# Revit family: Hager-Volta-IP30-Surface_mounted-syst-NoHosted-DE-de
name_source: partatom
category: Electrical Equipment
units: mm (PartAtom-declared; Revit-internal decimal feet)

## family parameters
Always vertical = Yes
Cut with Voids When Loaded = No
Panel Configuration = Two Columns, Circuits Across
Part Type = Panelboard
Room Calculation Point = No
Round Connector Dimension = Use Diameter
Shared = No
Work Plane-Based = Yes

## types (6) — shared parameters
Default Elevation = 1219 mm
EF000003 - Montageart = EV000384 - Aufputz
EF000007 - Farbe = EV000202 - weiß
EF000008 - Breite = 305 mm  [stored 1.00066 ft]
EF000049 - Tiefe = 96 mm  [stored 0.314961 ft]
EF000116 - RAL-Nummer = 9010
EF001062 - EMV-Ausführung = No
EF001088 - Anbaumöglichkeit = Yes
EF001131 - Innentiefe = 92 mm
EF001134 - DIN-Schiene = Yes
EF002950 - Breite in Teilungseinheiten = 12
EF005474 - Schutzart (IP) = EV006410 - IP30
EF006244 - Transparenter Deckel/Tür = No
EF006306 - Mit Schloss = No
EF009212 - Ausführung Deckel = EV009916 - mit Ausschnitt
EF015776 - Erdungsklemmenblock = No
EF015777 - Neutralleiterklemmenblock = No
EF015941 - Signaldurchlassende Tür = No
HG000001 - Anzahl der Spalten = 1
HG000003 - Bereich = Volta
HG000005 - Dicke = 3 mm  [stored 0.00984252 ft]
HG000006 - Unterputz = No
HG000009 - Doppelflügeligen Tür = No
HG000010 - Asymmetrische Türen = No
HG000011 - Leere Reihen von unten = No
HG000017 - Distanz zwischen den Polen = 18 mm  [stored 0.0590551 ft]
Manufacturer = Hager
Type Comments = Volta
zero-valued in all types: EF000218 - Einbautiefe, EF000332 - Einbauhöhe, EF000846 - Einbaubreite, HG000007 - Anzahl der leeren Spalten, HG000008 - Anzahl der leeren Reihen

## per-type parameters (varying)
| type | EF000040 - Höhe | EF000118 - Mit Montageplatte | EF000266 - Anzahl der Reihen | EF000339 - Art der Abdeckung | EF001596 - Werkstoff des Gehäuses | EF004462 - Art der Schließung | HG000002 - Mit tür | HG000004 - Herstellerreferenz | Model |
| Aufputz IP30 B305 H245 T96.5 12 Teilungseinheiten - VA12CN | 245 mm | No | 1 | EV000494 - ohne | EV000139 - Kunststoff |  | No | VA12CN | VA12CN |
| Aufputz IP30 B305 H370 T96.5 12 Teilungseinheiten - VA24CN | 370 mm | No | 2 | EV000494 - ohne | EV000139 - Kunststoff |  | No | VA24CN | VA24CN |
| Aufputz IP30 B305 H515 T96.5 12 Teilungseinheiten - VA36APZ | 515 mm | Yes | 3 | EV004216 - Tür | EV000154 - sonstige | EV000154 - sonstige | Yes | VA36APZ | VA36APZ |
| Aufputz IP30 B305 H515 T96.5 12 Teilungseinheiten - VA36CN | 515 mm | No | 3 | EV000494 - ohne | EV000139 - Kunststoff |  | No | VA36CN | VA36CN |
| Aufputz IP30 B305 H640 T96.5 12 Teilungseinheiten - VA48CK | 640 mm  [stored 2.09974 ft] | No | 4 | EV000494 - ohne | EV000139 - Kunststoff |  | No | VA48CK | VA48CK |
| Aufputz IP30 B305 H640 T96.5 12 Teilungseinheiten - VA48CN | 640 mm  [stored 2.09974 ft] | No | 4 | EV000494 - ohne | EV000139 - Kunststoff |  | No | VA48CN | VA48CN |

note: [stored X ft] marks values corroborated as IEEE doubles in the binary element streams (Revit-internal decimal feet)

## geometry (parser evidence)
native form markers: Sweep x13
no freeform markers — native parametric forms only
